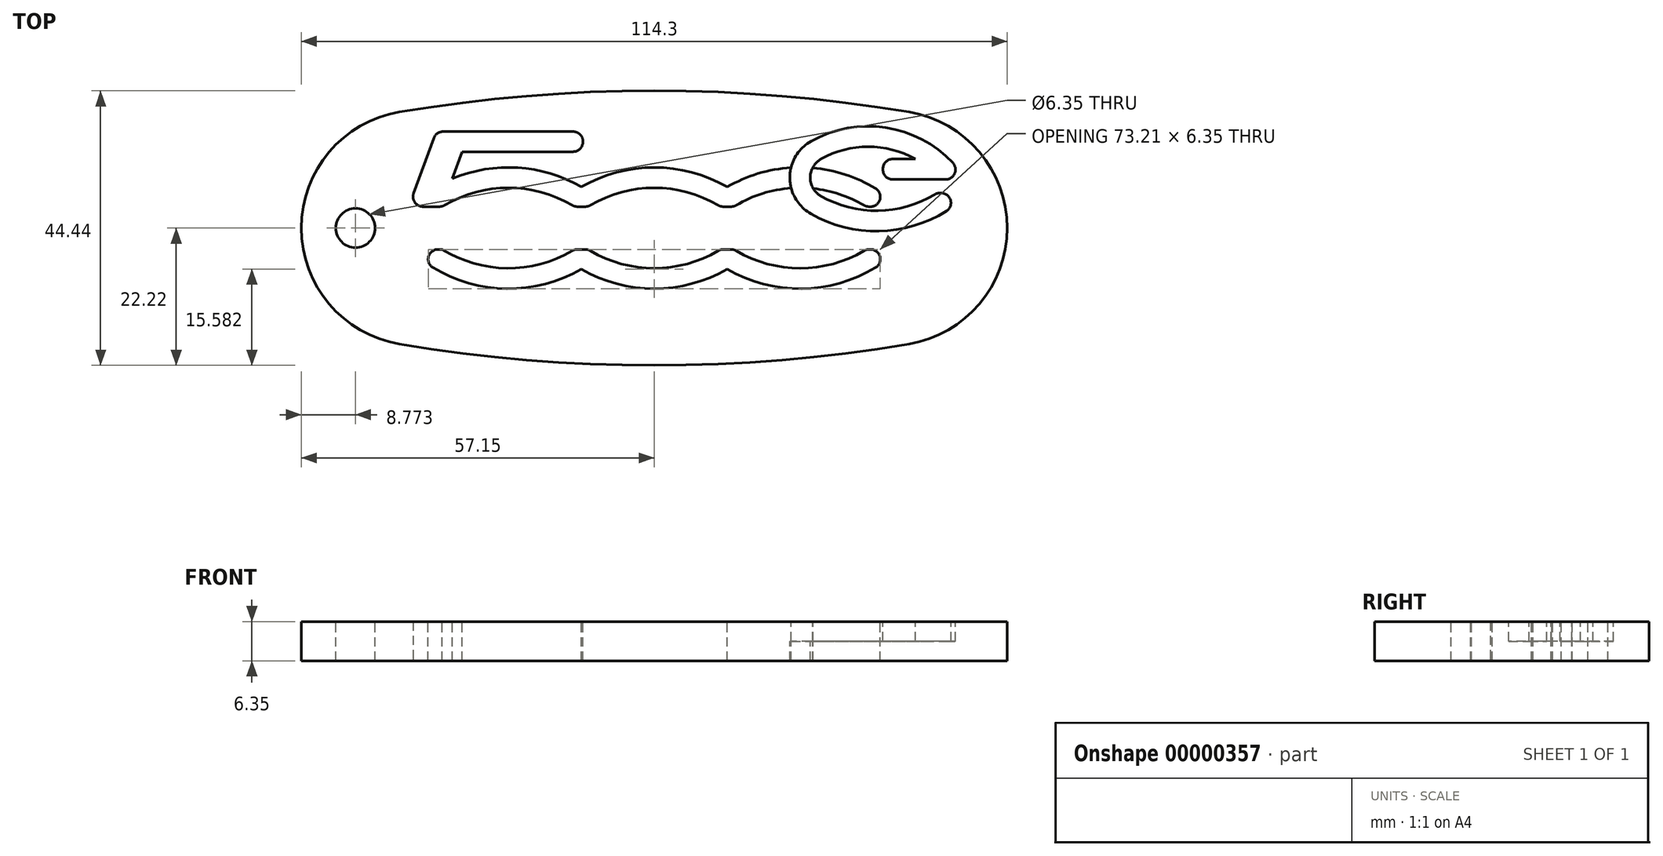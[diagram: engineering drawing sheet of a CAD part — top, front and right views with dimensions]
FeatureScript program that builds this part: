
annotation { "Feature Type Name" : "Feature", "Feature Type Description" : "" }
export const myFeature = defineFeature(function(context is Context, id is Id, definition is map)
    precondition{}
    {
        {
            var Q0;
            Q0=qCreatedBy(makeId("Top.planeOp"),FACE);
            var sketch = newSketch(context, id + "F0", { "sketchPlane" : qUnion([Q0])});
            skArc(sketch, "E0", {"start": v(-41.25, 18.79) * mm, "mid": v(-57.15, 0) * mm, "end": v(-41.25, -18.79) * mm});
            skArc(sketch, "E1", {"start": v(0, 22.22) * mm, "mid": v(-20.7, 21.36) * mm, "end": v(-41.25, 18.79) * mm});
            skLineSegment(sketch, "E2", {"start": v(0, 22.23) * mm, "end": v(0, 0) * mm, "construction": true});
            skLineSegment(sketch, "E3", {"start": v(0, 0) * mm, "end": v(-57.15, 0) * mm, "construction": true});
            skArc(sketch, "E4.0.MirrorCS", {"start": v(0, 22.22) * mm, "mid": v(20.7, 21.36) * mm, "end": v(41.25, 18.79) * mm});
            skArc(sketch, "E4.1.MirrorCS", {"start": v(41.25, 18.79) * mm, "mid": v(57.15, 0) * mm, "end": v(41.25, -18.79) * mm});
            skArc(sketch, "E5.0.MirrorCS", {"start": v(0, -22.22) * mm, "mid": v(-20.7, -21.36) * mm, "end": v(-41.25, -18.79) * mm});
            skArc(sketch, "E6.0.MirrorCS", {"start": v(0, -22.22) * mm, "mid": v(20.7, -21.36) * mm, "end": v(41.25, -18.79) * mm});
            skCircle(sketch, "E7", {"center": v(-48.38, 0) * mm, "radius": 3.18 * mm});
            skSolve(sketch);
        }
        {
            var Q0;
            Q0=qCreatedBy(makeId("Top.planeOp"),FACE);
            var sketch = newSketch(context, id + "F1", { "sketchPlane" : qUnion([Q0])});
            skLineSegment(sketch, "E8", {"start": v(-11.24, 15.6) * mm, "end": v(-35.32, 15.6) * mm});
            skLineSegment(sketch, "E9", {"start": v(-35.32, 15.6) * mm, "end": v(-39.74, 3.46) * mm});
            skLineSegment(sketch, "E10", {"start": v(-39.74, 3.46) * mm, "end": v(-34.33, 3.46) * mm});
            skArc(sketch, "E11", {"start": v(-39.74, -3.46) * mm, "mid": v(-26.3, -9.66) * mm, "end": v(-11.81, -6.65) * mm});
            skArc(sketch, "E12", {"start": v(-34.33, -3.46) * mm, "mid": v(-23.62, -6.51) * mm, "end": v(-12.91, -3.46) * mm});
            skLineSegment(sketch, "E13", {"start": v(-11.81, -6.65) * mm, "end": v(-11.81, -0.27) * mm, "construction": true});
            skLineSegment(sketch, "E14", {"start": v(11.81, -6.65) * mm, "end": v(11.81, -0.27) * mm, "construction": true});
            skLineSegment(sketch, "E15", {"start": v(-11.81, -0.27) * mm, "end": v(11.81, -0.27) * mm, "construction": true});
            skPoint(sketch, "E16", {"position": v(0, -0.27) * mm});
            skLineSegment(sketch, "E17", {"start": v(-39.74, -3.46) * mm, "end": v(-34.33, -3.46) * mm});
            skLineSegment(sketch, "E18", {"start": v(-12.91, -3.46) * mm, "end": v(-11.81, -3.46) * mm});
            skArc(sketch, "E19", {"start": v(-11.81, -6.65) * mm, "mid": v(0, -9.81) * mm, "end": v(11.81, -6.65) * mm});
            skArc(sketch, "E20.0.MirrorCS", {"start": v(10.7, -3.46) * mm, "mid": v(0, -6.51) * mm, "end": v(-10.7, -3.46) * mm});
            skLineSegment(sketch, "E20.1.MirrorCS", {"start": v(-10.7, -3.46) * mm, "end": v(-11.81, -3.46) * mm});
            skLineSegment(sketch, "E21.0.MirrorCS", {"start": v(39.74, -3.46) * mm, "end": v(34.33, -3.46) * mm});
            skArc(sketch, "E21.1.MirrorCS", {"start": v(39.74, -3.46) * mm, "mid": v(26.3, -9.66) * mm, "end": v(11.81, -6.65) * mm});
            skArc(sketch, "E21.2.MirrorCS", {"start": v(34.33, -3.46) * mm, "mid": v(23.62, -6.51) * mm, "end": v(12.91, -3.46) * mm});
            skLineSegment(sketch, "E21.3.MirrorCS", {"start": v(12.91, -3.46) * mm, "end": v(11.81, -3.46) * mm});
            skLineSegment(sketch, "E21.4.MirrorCS", {"start": v(10.7, -3.46) * mm, "end": v(11.81, -3.46) * mm});
            skLineSegment(sketch, "E22.0.MirrorCS", {"start": v(39.74, 3.46) * mm, "end": v(34.33, 3.46) * mm});
            skLineSegment(sketch, "E22.1.MirrorCS", {"start": v(10.7, 3.46) * mm, "end": v(11.81, 3.46) * mm});
            skLineSegment(sketch, "E22.2.MirrorCS", {"start": v(12.91, 3.46) * mm, "end": v(11.81, 3.46) * mm});
            skArc(sketch, "E22.3.MirrorCS", {"start": v(34.33, 3.46) * mm, "mid": v(23.62, 6.51) * mm, "end": v(12.91, 3.46) * mm});
            skArc(sketch, "E22.4.MirrorCS", {"start": v(39.74, 3.46) * mm, "mid": v(26.3, 9.66) * mm, "end": v(11.81, 6.65) * mm});
            skArc(sketch, "E22.5.MirrorCS", {"start": v(10.7, 3.46) * mm, "mid": v(0, 6.51) * mm, "end": v(-10.7, 3.46) * mm});
            skArc(sketch, "E22.6.MirrorCS", {"start": v(-11.81, 6.65) * mm, "mid": v(0, 9.81) * mm, "end": v(11.81, 6.65) * mm});
            skLineSegment(sketch, "E22.7.MirrorCS", {"start": v(-10.7, 3.46) * mm, "end": v(-11.81, 3.46) * mm});
            skLineSegment(sketch, "E22.8.MirrorCS", {"start": v(-12.91, 3.46) * mm, "end": v(-11.81, 3.46) * mm});
            skArc(sketch, "E22.9.MirrorCS", {"start": v(-39.74, 3.46) * mm, "mid": v(-26.3, 9.66) * mm, "end": v(-11.81, 6.65) * mm});
            skArc(sketch, "E22.10.MirrorCS", {"start": v(-34.33, 3.46) * mm, "mid": v(-23.62, 6.51) * mm, "end": v(-12.91, 3.46) * mm});
            skLineSegment(sketch, "E23", {"start": v(-11.24, 15.6) * mm, "end": v(-11.81, 12.35) * mm});
            skLineSegment(sketch, "E24", {"start": v(-11.81, 12.35) * mm, "end": v(-31.1, 12.35) * mm});
            skLineSegment(sketch, "E25", {"start": v(-31.1, 12.35) * mm, "end": v(-34.33, 3.46) * mm});
            skSolve(sketch);
        }
        {
            var Q0;
            Q0=qCreatedBy(makeId("Top.planeOp"),FACE);
            var sketch = newSketch(context, id + "F2", { "sketchPlane" : qUnion([Q0])});
            skLineSegment(sketch, "E26", {"start": v(50.45, 8.16) * mm, "end": v(23.62, 8.16) * mm, "construction": true});
            skLineSegment(sketch, "E27", {"start": v(37.03, 16.33) * mm, "end": v(37.03, 0) * mm, "construction": true});
            skPoint(sketch, "E28", {"position": v(37.03, 8.16) * mm});
            skPoint(sketch, "E29", {"position": v(37.03, 3.46) * mm});
            skLineSegment(sketch, "E30", {"start": v(23.62, 9.81) * mm, "end": v(23.62, 6.51) * mm, "construction": true});
            skArc(sketch, "E31", {"start": v(50.45, 7.86) * mm, "mid": v(39.14, 15.93) * mm, "end": v(25.38, 14.03) * mm});
            skLineSegment(sketch, "E32", {"start": v(50.45, 7.86) * mm, "end": v(37.03, 7.86) * mm});
            skLineSegment(sketch, "E33", {"start": v(37.03, 7.86) * mm, "end": v(37.03, 11.16) * mm});
            skLineSegment(sketch, "E34", {"start": v(37.03, 11.16) * mm, "end": v(42.29, 11.16) * mm});
            skArc(sketch, "E35", {"start": v(42.29, 11.16) * mm, "mid": v(34.64, 13.18) * mm, "end": v(27, 11.16) * mm});
            skArc(sketch, "E36", {"start": v(25.38, 14.03) * mm, "mid": v(21.96, 8.16) * mm, "end": v(25.38, 2.3) * mm});
            skArc(sketch, "E37", {"start": v(27, 11.16) * mm, "mid": v(25.26, 8.16) * mm, "end": v(27, 5.16) * mm});
            skArc(sketch, "E38", {"start": v(25.38, 2.3) * mm, "mid": v(38.77, -0.32) * mm, "end": v(51.04, 5.66) * mm});
            skArc(sketch, "E39", {"start": v(27, 5.16) * mm, "mid": v(36.45, 2.8) * mm, "end": v(45.76, 5.66) * mm});
            skLineSegment(sketch, "E40", {"start": v(51.04, 5.66) * mm, "end": v(45.76, 5.66) * mm});
            skSolve(sketch);
        }
        {
            var Q0;
            Q0=makeQuery(id+"F0.imprint","IMPRINT",FACE,{"disambiguationData":[TD([[makeQuery(id+"F0.imprint","IMPRINT",EDGE,{"derivedFrom":sQuery(id+"F0.wireOp",EDGE,"E0")}),1.0]])]});
            extrude(context, id + "F3", {"entities" : qUnion([Q0]), "oppositeDirection" : true, "depth" : 6.35 * mm});
        }
        {
            var Q0;
            Q0=makeQuery(id+"F1.imprint","IMPRINT",FACE,{"disambiguationData":[TD([[makeQuery(id+"F1.imprint","IMPRINT",EDGE,{"derivedFrom":sQuery(id+"F1.wireOp",EDGE,"E8")}),1.0]])]});
            var Q1;
            {var subQ3=sQuery(id+"F1.wireOp",EDGE,"E10");Q1=makeQuery(id+"F1.imprint","IMPRINT",FACE,{"disambiguationData":[TD([[makeQuery(id+"F1.imprint","IMPRINT",EDGE,{"derivedFrom":subQ3}),1.0]])]});}
            var Q2;
            Q2=makeQuery(id+"F1.imprint","IMPRINT",FACE,{"disambiguationData":[TD([[makeQuery(id+"F1.imprint","IMPRINT",EDGE,{"derivedFrom":sQuery(id+"F1.wireOp",EDGE,"E22.0.MirrorCS")}),-1.0]])]});
            var Q3;
            Q3=makeQuery(id+"F1.imprint","IMPRINT",FACE,{"disambiguationData":[TD([[makeQuery(id+"F1.imprint","IMPRINT",EDGE,{"derivedFrom":sQuery(id+"F1.wireOp",EDGE,"E11")}),1.0]])]});
            extrude(context, id + "F4", {"entities" : qUnion([Q0, Q1, Q2, Q3]), "operationType" : NewBodyOperationType.REMOVE, "endBound" : BoundingType.UP_TO_NEXT, "oppositeDirection" : true, "depth" : 25.4 * mm});
        }
        {
            var Q0;
            Q0=makeQuery(id+"F2.imprint","IMPRINT",FACE,{"disambiguationData":[TD([[makeQuery(id+"F2.imprint","IMPRINT",EDGE,{"derivedFrom":sQuery(id+"F2.wireOp",EDGE,"E31")}),1.0]])]});
            var Q1;
            Q1=makeQuery(id+"F3.opExtrude","CAP_FACE",FACE,{"disambiguationData":[OSD([sQuery(id+"F0.wireOp",EDGE,"E0"),sQuery(id+"F0.wireOp",EDGE,"E4.1.MirrorCS"),sQuery(id+"F0.wireOp",EDGE,"E1"),sQuery(id+"F0.wireOp",EDGE,"E5.0.MirrorCS"),sQuery(id+"F0.wireOp",EDGE,"E7")])],"isStart":false});
            extrude(context, id + "F5", {"entities" : qUnion([Q0]), "operationType" : NewBodyOperationType.ADD, "endBound" : BoundingType.UP_TO_SURFACE, "oppositeDirection" : true, "endBoundEntityFace" : qUnion([Q1]), "depth" : 25.4 * mm});
        }
        {
            var Q0;
            Q0=makeQuery(id+"F2.imprint","IMPRINT",FACE,{"disambiguationData":[TD([[makeQuery(id+"F2.imprint","IMPRINT",EDGE,{"derivedFrom":sQuery(id+"F2.wireOp",EDGE,"E31")}),1.0]])]});
            extrude(context, id + "F6", {"entities" : qUnion([Q0]), "operationType" : NewBodyOperationType.REMOVE, "oppositeDirection" : true, "depth" : 3.17 * mm});
        }
        {
            var Q0;
            Q0=makeQuery(id+"F6.boolean.opBoolean","COPY",EDGE,{"derivedFrom":makeQuery(id+"F6.opExtrude","SWEPT_EDGE",EDGE,{"disambiguationData":[OSD([sQuery(id+"F2.wireOp",EDGE,"E31"),sQuery(id+"F2.wireOp",EDGE,"E32")])]})});
            var Q1;
            Q1=makeQuery(id+"F6.boolean.opBoolean","COPY",EDGE,{"derivedFrom":makeQuery(id+"F6.opExtrude","SWEPT_EDGE",EDGE,{"disambiguationData":[OSD([sQuery(id+"F2.wireOp",EDGE,"E32"),sQuery(id+"F2.wireOp",EDGE,"E33")])]})});
            var Q2;
            Q2=makeQuery(id+"F6.boolean.opBoolean","COPY",EDGE,{"derivedFrom":makeQuery(id+"F6.opExtrude","SWEPT_EDGE",EDGE,{"disambiguationData":[OSD([sQuery(id+"F2.wireOp",EDGE,"E33"),sQuery(id+"F2.wireOp",EDGE,"E34")])]})});
            var Q3;
            Q3=makeQuery(id+"F6.boolean.opBoolean","COPY",EDGE,{"derivedFrom":makeQuery(id+"F6.opExtrude","SWEPT_EDGE",EDGE,{"disambiguationData":[OSD([sQuery(id+"F2.wireOp",EDGE,"E38"),sQuery(id+"F2.wireOp",EDGE,"E40")])]})});
            var Q4;
            Q4=makeQuery(id+"F6.boolean.opBoolean","COPY",EDGE,{"derivedFrom":makeQuery(id+"F6.opExtrude","SWEPT_EDGE",EDGE,{"disambiguationData":[OSD([sQuery(id+"F2.wireOp",EDGE,"E39"),sQuery(id+"F2.wireOp",EDGE,"E40")])]})});
            var Q5;
            Q5=makeQuery(id+"F4.boolean.opBoolean","COPY",EDGE,{"derivedFrom":makeQuery(id+"F4.opExtrude","SWEPT_EDGE",EDGE,{"disambiguationData":[OSD([sQuery(id+"F1.wireOp",EDGE,"E21.0.MirrorCS"),sQuery(id+"F1.wireOp",EDGE,"E21.2.MirrorCS")])]})});
            var Q6;
            Q6=makeQuery(id+"F4.boolean.opBoolean","COPY",EDGE,{"derivedFrom":makeQuery(id+"F4.opExtrude","SWEPT_EDGE",EDGE,{"disambiguationData":[OSD([sQuery(id+"F1.wireOp",EDGE,"E21.0.MirrorCS"),sQuery(id+"F1.wireOp",EDGE,"E21.1.MirrorCS")])]})});
            var Q7;
            Q7=makeQuery(id+"F4.boolean.opBoolean","COPY",EDGE,{"derivedFrom":makeQuery(id+"F4.opExtrude","SWEPT_EDGE",EDGE,{"disambiguationData":[OSD([sQuery(id+"F1.wireOp",EDGE,"E20.0.MirrorCS"),sQuery(id+"F1.wireOp",EDGE,"E21.4.MirrorCS")])]})});
            var Q8;
            Q8=makeQuery(id+"F4.boolean.opBoolean","COPY",EDGE,{"derivedFrom":makeQuery(id+"F4.opExtrude","SWEPT_EDGE",EDGE,{"disambiguationData":[OSD([sQuery(id+"F1.wireOp",EDGE,"E21.2.MirrorCS"),sQuery(id+"F1.wireOp",EDGE,"E21.3.MirrorCS")])]})});
            var Q9;
            Q9=makeQuery(id+"F4.boolean.opBoolean","COPY",EDGE,{"derivedFrom":makeQuery(id+"F4.opExtrude","SWEPT_EDGE",EDGE,{"disambiguationData":[OSD([sQuery(id+"F1.wireOp",EDGE,"E12"),sQuery(id+"F1.wireOp",EDGE,"E18")])]})});
            var Q10;
            Q10=makeQuery(id+"F4.boolean.opBoolean","COPY",EDGE,{"derivedFrom":makeQuery(id+"F4.opExtrude","SWEPT_EDGE",EDGE,{"disambiguationData":[OSD([sQuery(id+"F1.wireOp",EDGE,"E20.0.MirrorCS"),sQuery(id+"F1.wireOp",EDGE,"E20.1.MirrorCS")])]})});
            var Q11;
            Q11=makeQuery(id+"F4.boolean.opBoolean","COPY",EDGE,{"derivedFrom":makeQuery(id+"F4.opExtrude","SWEPT_EDGE",EDGE,{"disambiguationData":[OSD([sQuery(id+"F1.wireOp",EDGE,"E11"),sQuery(id+"F1.wireOp",EDGE,"E17")])]})});
            var Q12;
            Q12=makeQuery(id+"F4.boolean.opBoolean","COPY",EDGE,{"derivedFrom":makeQuery(id+"F4.opExtrude","SWEPT_EDGE",EDGE,{"disambiguationData":[OSD([sQuery(id+"F1.wireOp",EDGE,"E9"),sQuery(id+"F1.wireOp",EDGE,"E10"),sQuery(id+"F1.wireOp",EDGE,"E22.9.MirrorCS")])]})});
            var Q13;
            Q13=makeQuery(id+"F4.boolean.opBoolean","COPY",EDGE,{"derivedFrom":makeQuery(id+"F4.opExtrude","SWEPT_EDGE",EDGE,{"disambiguationData":[OSD([sQuery(id+"F1.wireOp",EDGE,"E8"),sQuery(id+"F1.wireOp",EDGE,"E9")])]})});
            var Q14;
            Q14=makeQuery(id+"F4.boolean.opBoolean","COPY",EDGE,{"derivedFrom":makeQuery(id+"F4.opExtrude","SWEPT_EDGE",EDGE,{"disambiguationData":[OSD([sQuery(id+"F1.wireOp",EDGE,"E8"),sQuery(id+"F1.wireOp",EDGE,"E23")])]})});
            var Q15;
            Q15=makeQuery(id+"F4.boolean.opBoolean","COPY",EDGE,{"derivedFrom":makeQuery(id+"F4.opExtrude","SWEPT_EDGE",EDGE,{"disambiguationData":[OSD([sQuery(id+"F1.wireOp",EDGE,"E23"),sQuery(id+"F1.wireOp",EDGE,"E24")])]})});
            var Q16;
            Q16=makeQuery(id+"F4.boolean.opBoolean","COPY",EDGE,{"derivedFrom":makeQuery(id+"F4.opExtrude","SWEPT_EDGE",EDGE,{"disambiguationData":[OSD([sQuery(id+"F1.wireOp",EDGE,"E22.8.MirrorCS"),sQuery(id+"F1.wireOp",EDGE,"E22.10.MirrorCS")])]})});
            var Q17;
            Q17=makeQuery(id+"F4.boolean.opBoolean","COPY",EDGE,{"derivedFrom":makeQuery(id+"F4.opExtrude","SWEPT_EDGE",EDGE,{"disambiguationData":[OSD([sQuery(id+"F1.wireOp",EDGE,"E22.5.MirrorCS"),sQuery(id+"F1.wireOp",EDGE,"E22.7.MirrorCS")])]})});
            var Q18;
            Q18=makeQuery(id+"F4.boolean.opBoolean","COPY",EDGE,{"derivedFrom":makeQuery(id+"F4.opExtrude","SWEPT_EDGE",EDGE,{"disambiguationData":[OSD([sQuery(id+"F1.wireOp",EDGE,"E22.1.MirrorCS"),sQuery(id+"F1.wireOp",EDGE,"E22.5.MirrorCS")])]})});
            var Q19;
            Q19=makeQuery(id+"F4.boolean.opBoolean","COPY",EDGE,{"derivedFrom":makeQuery(id+"F4.opExtrude","SWEPT_EDGE",EDGE,{"disambiguationData":[OSD([sQuery(id+"F1.wireOp",EDGE,"E22.2.MirrorCS"),sQuery(id+"F1.wireOp",EDGE,"E22.3.MirrorCS")])]})});
            var Q20;
            Q20=makeQuery(id+"F4.boolean.opBoolean","COPY",EDGE,{"derivedFrom":makeQuery(id+"F4.opExtrude","SWEPT_EDGE",EDGE,{"disambiguationData":[OSD([sQuery(id+"F1.wireOp",EDGE,"E22.0.MirrorCS"),sQuery(id+"F1.wireOp",EDGE,"E22.3.MirrorCS")])]})});
            var Q21;
            Q21=makeQuery(id+"F4.boolean.opBoolean","COPY",EDGE,{"derivedFrom":makeQuery(id+"F4.opExtrude","SWEPT_EDGE",EDGE,{"disambiguationData":[OSD([sQuery(id+"F1.wireOp",EDGE,"E22.0.MirrorCS"),sQuery(id+"F1.wireOp",EDGE,"E22.4.MirrorCS")])]})});
            var Q22;
            Q22=makeQuery(id+"F4.boolean.opBoolean","COPY",EDGE,{"derivedFrom":makeQuery(id+"F4.opExtrude","SWEPT_EDGE",EDGE,{"disambiguationData":[OSD([sQuery(id+"F1.wireOp",EDGE,"E10"),sQuery(id+"F1.wireOp",EDGE,"E22.10.MirrorCS"),sQuery(id+"F1.wireOp",EDGE,"E25")])]})});
            fillet(context, id + "F7", {"entities" : qUnion([Q0, Q1, Q2, Q3, Q4, Q5, Q6, Q7, Q8, Q9, Q10, Q11, Q12, Q13, Q14, Q15, Q16, Q17, Q18, Q19, Q20, Q21, Q22]), "radius" : 1.59 * mm, "tangentPropagation" : true, "allowEdgeOverflow" : false});
        }
    });
